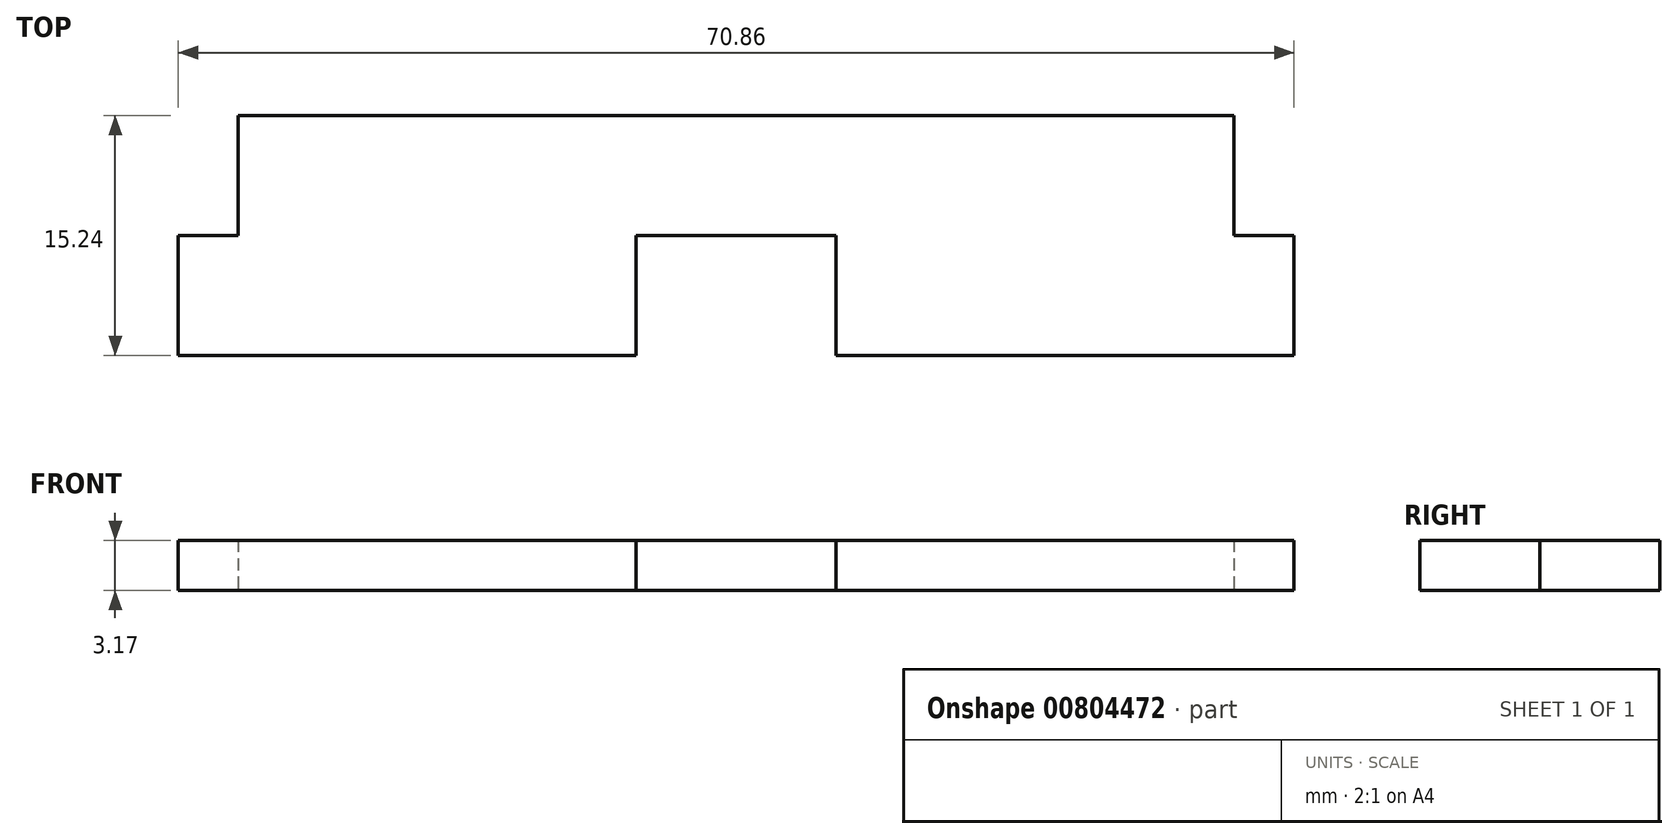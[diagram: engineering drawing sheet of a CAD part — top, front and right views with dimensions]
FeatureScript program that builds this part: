
annotation { "Feature Type Name" : "Feature", "Feature Type Description" : "" }
export const myFeature = defineFeature(function(context is Context, id is Id, definition is map)
    precondition{}
    {
        {
            var Q0;
            Q0=qCreatedBy(makeId("Top.planeOp"),FACE);
            var sketch = newSketch(context, id + "F0", { "sketchPlane" : qUnion([Q0])});
            skLineSegment(sketch, "E0", {"start": v(-31.62, 0) * mm, "end": v(-31.62, 7.62) * mm});
            skLineSegment(sketch, "E1", {"start": v(-31.62, 7.62) * mm, "end": v(31.62, 7.62) * mm});
            skLineSegment(sketch, "E2", {"start": v(31.62, 7.62) * mm, "end": v(31.62, 0) * mm});
            skLineSegment(sketch, "E3", {"start": v(31.62, 0) * mm, "end": v(35.43, 0) * mm});
            skLineSegment(sketch, "E4", {"start": v(35.43, 0) * mm, "end": v(35.43, -7.62) * mm});
            skLineSegment(sketch, "E5", {"start": v(35.43, -7.62) * mm, "end": v(-35.43, -7.62) * mm});
            skLineSegment(sketch, "E6", {"start": v(-35.43, -7.62) * mm, "end": v(-35.43, 0) * mm});
            skLineSegment(sketch, "E7", {"start": v(-35.43, 0) * mm, "end": v(-31.62, 0) * mm});
            skLineSegment(sketch, "E8", {"start": v(0, 7.62) * mm, "end": v(0, 0) * mm, "construction": true});
            skLineSegment(sketch, "E9.bottom", {"start": v(6.35, 0) * mm, "end": v(-6.35, 0) * mm});
            skLineSegment(sketch, "E9.top", {"start": v(6.35, -15.24) * mm, "end": v(-6.35, -15.24) * mm});
            skLineSegment(sketch, "E9.left", {"start": v(6.35, 0) * mm, "end": v(6.35, -15.24) * mm});
            skLineSegment(sketch, "E9.right", {"start": v(-6.35, 0) * mm, "end": v(-6.35, -15.24) * mm});
            skPoint(sketch, "E9.middle", {"position": v(0, -7.62) * mm});
            skSolve(sketch);
        }
        {
            var Q0;
            Q0=makeQuery(id+"F0.imprint","IMPRINT",FACE,{"disambiguationData":[TD([[makeQuery(id+"F0.imprint","IMPRINT",EDGE,{"derivedFrom":sQuery(id+"F0.wireOp",EDGE,"E0")}),-1.0]])]});
            extrude(context, id + "F1", {"entities" : qUnion([Q0]), "depth" : 3.17 * mm, "offsetDistance" : 25.4 * mm});
        }
    });
